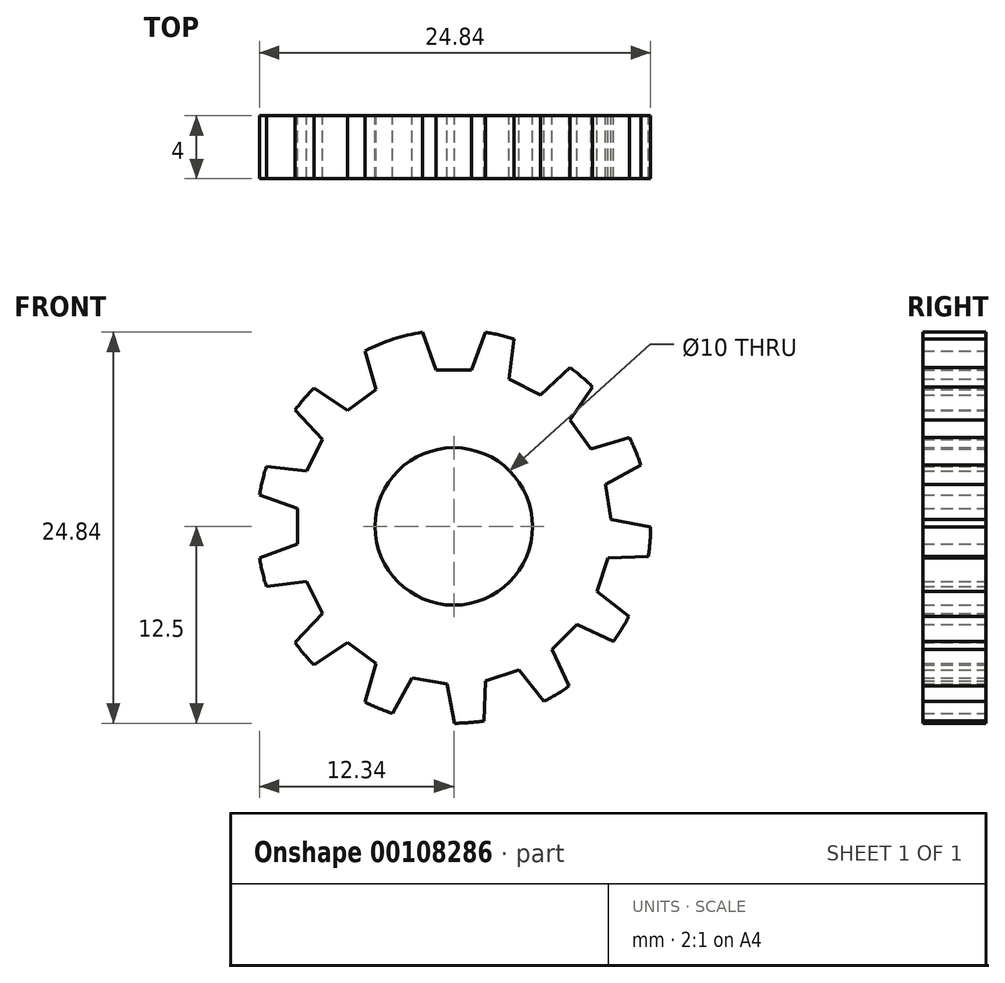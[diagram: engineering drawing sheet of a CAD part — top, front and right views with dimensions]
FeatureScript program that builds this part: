
annotation { "Feature Type Name" : "Feature", "Feature Type Description" : "" }
export const myFeature = defineFeature(function(context is Context, id is Id, definition is map)
    precondition{}
    {
        {
            assignVariable(context, id + "F0", {"name" : "Thickness", "anyValue" : 4});
        }
        {
            assignVariable(context, id + "F1", {"name" : "Pattern_Degrees", "anyValue" : 9});
        }
        {
            assignVariable(context, id + "F2", {"name" : "Tooth_Count", "anyValue" : 40});
        }
        {
            var Q0;
            Q0=qCreatedBy(makeId("Front.planeOp"),FACE);
            var sketch = newSketch(context, id + "F3", { "sketchPlane" : qUnion([Q0])});
            skCircle(sketch, "E0", {"center": v(0, 0) * mm, "radius": 12.5 * mm});
            skCircle(sketch, "E1", {"center": v(0, 0) * mm, "radius": 5 * mm});
            skCircle(sketch, "E2", {"center": v(0, 0) * mm, "radius": 10 * mm, "construction": true});
            skLineSegment(sketch, "E3", {"start": v(0, 0) * mm, "end": v(0, 12.5) * mm, "construction": true});
            skLineSegment(sketch, "E4", {"start": v(1.13, 9.94) * mm, "end": v(2, 12.34) * mm});
            skLineSegment(sketch, "E5.MirrorCS", {"start": v(-1.13, 9.94) * mm, "end": v(-2, 12.34) * mm});
            skLineSegment(sketch, "E6", {"start": v(-1.13, 9.94) * mm, "end": v(1.13, 9.94) * mm});
            skSolve(sketch);
        }
        {
            var Q0;
            Q0 = qSketchRegion(id + "F3", true);
            extrude(context, id + "F4", {"entities" : qUnion([Q0]), "depth" : (getVariable(context, 'Thickness')) * mm});
        }
        {
            var Q0;
            {var subQ0=sQuery(id+"F3.wireOp",EDGE,"E4");Q0=makeQuery(id+"F3.imprint","IMPRINT",FACE,{"disambiguationData":[TD([[makeQuery(id+"F3.imprint","IMPRINT",EDGE,{"derivedFrom":subQ0}),1.0]])]});}
            extrude(context, id + "F5", {"entities" : qUnion([Q0]), "operationType" : NewBodyOperationType.REMOVE, "depth" : (getVariable(context, 'Thickness') * 2) * mm});
        }
        {
            var Q0;
            Q0=makeQuery(id+"F4.opExtrude","SWEPT_BODY",BODY,{"disambiguationData":[OSD([sQuery(id+"F3.wireOp",EDGE,"E0"),sQuery(id+"F3.wireOp",EDGE,"E1")])]});
            var Q1;
            Q1=makeQuery(id+"F5.boolean.opBoolean","COPY",FACE,{"derivedFrom":makeQuery(id+"F5.opExtrude","SWEPT_FACE",FACE,{"disambiguationData":[OSD([sQuery(id+"F3.wireOp",EDGE,"E4")])]})});
            var Q2;
            Q2=makeQuery(id+"F5.boolean.opBoolean","COPY",FACE,{"derivedFrom":makeQuery(id+"F5.opExtrude","SWEPT_FACE",FACE,{"disambiguationData":[OSD([sQuery(id+"F3.wireOp",EDGE,"E6")])]})});
            var Q3;
            Q3=makeQuery(id+"F5.boolean.opBoolean","COPY",FACE,{"derivedFrom":makeQuery(id+"F5.opExtrude","SWEPT_FACE",FACE,{"disambiguationData":[OSD([sQuery(id+"F3.wireOp",EDGE,"E5.MirrorCS")])]})});
            var Q4;
            Q4=makeQuery(id+"F4.opExtrude","SWEPT_FACE",FACE,{"disambiguationData":[OSD([sQuery(id+"F3.wireOp",EDGE,"E0")])]});
            circularPattern(context, id + "F6", {"patternType" : PatternType.FACE, "faces" : qUnion([Q1, Q2, Q3]), "axis" : qUnion([Q4]), "angle" : (getVariable(context, 'Pattern_Degrees')) * degree, "instanceCount" : getVariable(context, 'Tooth_Count')});
        }
    });
